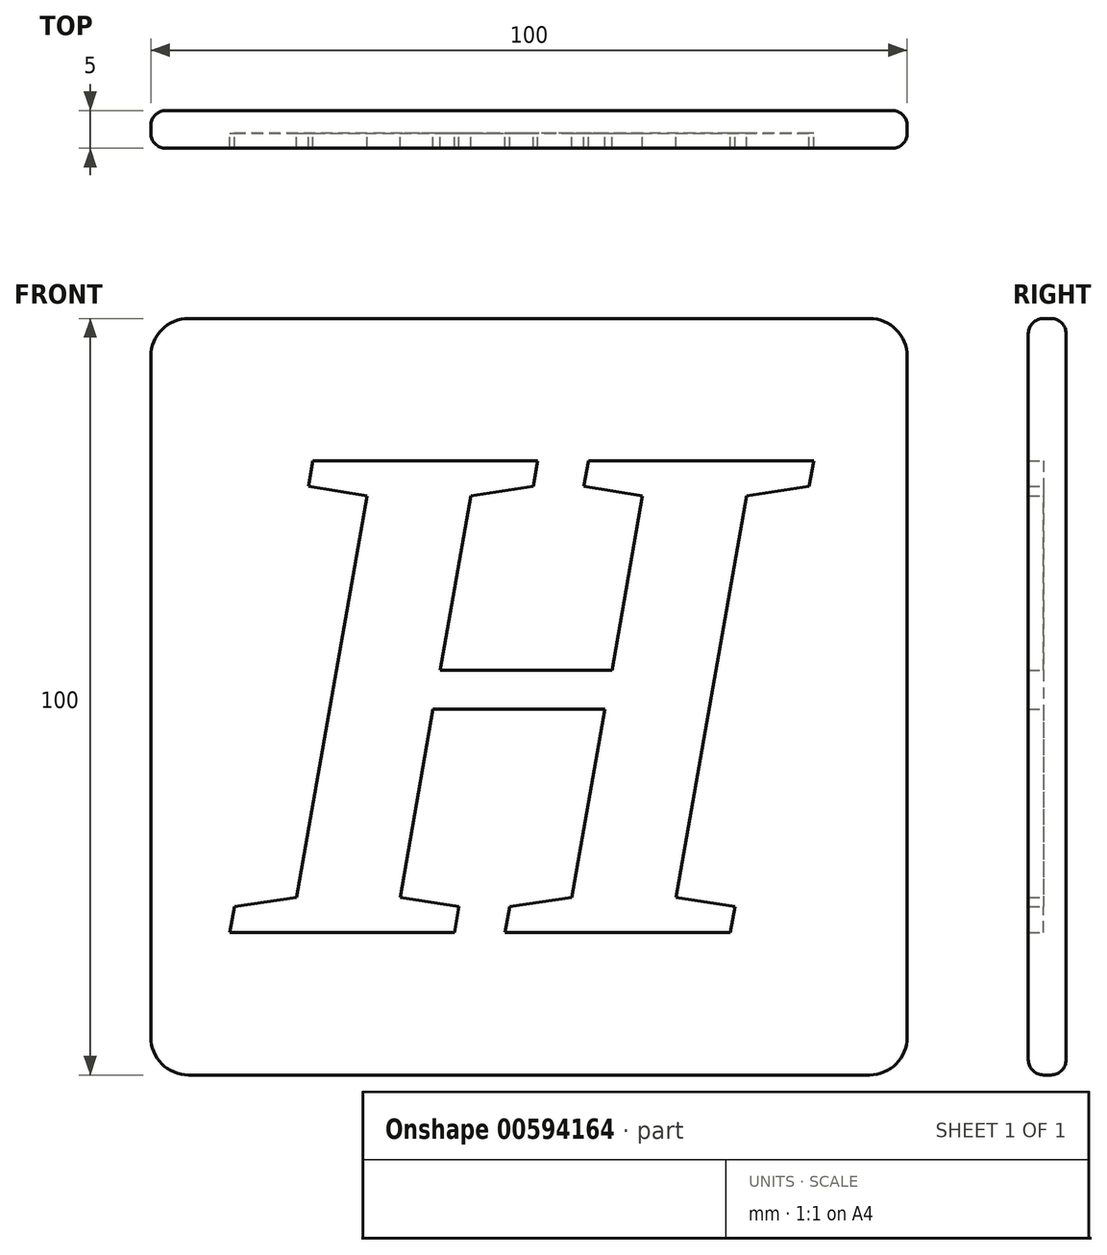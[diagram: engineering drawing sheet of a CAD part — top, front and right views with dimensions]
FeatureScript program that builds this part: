
annotation { "Feature Type Name" : "Feature", "Feature Type Description" : "" }
export const myFeature = defineFeature(function(context is Context, id is Id, definition is map)
    precondition{}
    {
        {
            var Q0;
            Q0=qCreatedBy(makeId("Front.planeOp"),FACE);
            var sketch = newSketch(context, id + "F0", { "sketchPlane" : qUnion([Q0])});
            skLineSegment(sketch, "E0.bottom", {"start": v(50, 50) * mm, "end": v(-50, 50) * mm});
            skLineSegment(sketch, "E0.top", {"start": v(50, -50) * mm, "end": v(-50, -50) * mm});
            skLineSegment(sketch, "E0.left", {"start": v(50, 50) * mm, "end": v(50, -50) * mm});
            skLineSegment(sketch, "E0.right", {"start": v(-50, 50) * mm, "end": v(-50, -50) * mm});
            skPoint(sketch, "E0.middle", {"position": v(0, 0) * mm});
            skSolve(sketch);
        }
        {
            var Q0;
            Q0=makeQuery(id+"F0.imprint","IMPRINT",FACE,{"disambiguationData":[TD([[makeQuery(id+"F0.imprint","IMPRINT",EDGE,{"derivedFrom":sQuery(id+"F0.wireOp",EDGE,"E0.bottom")}),1.0]])]});
            extrude(context, id + "F1", {"entities" : qUnion([Q0]), "depth" : 5 * mm, "offsetDistance" : 25 * mm});
        }
        {
            var Q0;
            Q0=makeQuery(id+"F1.opExtrude","SWEPT_EDGE",EDGE,{"disambiguationData":[OSD([sQuery(id+"F0.wireOp",EDGE,"E0.bottom"),sQuery(id+"F0.wireOp",EDGE,"E0.left")])]});
            var Q1;
            Q1=makeQuery(id+"F1.opExtrude","SWEPT_EDGE",EDGE,{"disambiguationData":[OSD([sQuery(id+"F0.wireOp",EDGE,"E0.bottom"),sQuery(id+"F0.wireOp",EDGE,"E0.right")])]});
            var Q2;
            Q2=makeQuery(id+"F1.opExtrude","SWEPT_EDGE",EDGE,{"disambiguationData":[OSD([sQuery(id+"F0.wireOp",EDGE,"E0.top"),sQuery(id+"F0.wireOp",EDGE,"E0.right")])]});
            var Q3;
            Q3=makeQuery(id+"F1.opExtrude","SWEPT_EDGE",EDGE,{"disambiguationData":[OSD([sQuery(id+"F0.wireOp",EDGE,"E0.top"),sQuery(id+"F0.wireOp",EDGE,"E0.left")])]});
            fillet(context, id + "F2", {"entities" : qUnion([Q0, Q1, Q2, Q3]), "radius" : 5 * mm, "tangentPropagation" : true, "allowEdgeOverflow" : false});
        }
        {
            var Q0;
            Q0=makeQuery(id+"F1.opExtrude","CAP_FACE",FACE,{"disambiguationData":[OSD([sQuery(id+"F0.wireOp",EDGE,"E0.bottom"),sQuery(id+"F0.wireOp",EDGE,"E0.top"),sQuery(id+"F0.wireOp",EDGE,"E0.left"),sQuery(id+"F0.wireOp",EDGE,"E0.right")])],"isStart":false});
            var Q1;
            Q1=makeQuery(id+"F1.opExtrude","CAP_FACE",FACE,{"disambiguationData":[OSD([sQuery(id+"F0.wireOp",EDGE,"E0.bottom"),sQuery(id+"F0.wireOp",EDGE,"E0.top"),sQuery(id+"F0.wireOp",EDGE,"E0.left"),sQuery(id+"F0.wireOp",EDGE,"E0.right")])],"isStart":true});
            fillet(context, id + "F3", {"entities" : qUnion([Q0, Q1]), "radius" : 2 * mm, "tangentPropagation" : true, "allowEdgeOverflow" : false});
        }
        {
            var Q0;
            Q0=makeQuery(id+"F1.opExtrude","CAP_FACE",FACE,{"disambiguationData":[OSD([sQuery(id+"F0.wireOp",EDGE,"E0.bottom"),sQuery(id+"F0.wireOp",EDGE,"E0.top"),sQuery(id+"F0.wireOp",EDGE,"E0.left"),sQuery(id+"F0.wireOp",EDGE,"E0.right")])],"isStart":false});
            var sketch = newSketch(context, id + "F4", { "sketchPlane" : qUnion([Q0])});
            skText(sketch, "E1", { "text": "H", "fontName": "Tinos-BoldItalic.ttf"});
            const initialGuessF4  = {"E1": [-0.03885, -0.03116, 1, 0, 0.06857]};
            skSetInitialGuess(sketch, initialGuessF4);
            skSolve(sketch);
        }
        {
            var Q0;
            Q0=makeQuery(id+"F4.imprint","IMPRINT",FACE,{"disambiguationData":[TD([[makeQuery(id+"F4.imprint","IMPRINT",EDGE,{"derivedFrom":sQuery(id+"F4.wireOp",EDGE,"E1.sketch_text.stroke-0")}),-1.0]])]});
            extrude(context, id + "F5", {"entities" : qUnion([Q0]), "operationType" : NewBodyOperationType.REMOVE, "oppositeDirection" : true, "depth" : 2 * mm, "offsetDistance" : 25 * mm});
        }
        {
            var Q0;
            Q0=makeQuery(id+"F5.boolean.opBoolean","COPY",FACE,{"derivedFrom":makeQuery(id+"F5.opExtrude","CAP_FACE",FACE,{"disambiguationData":[OSD([sQuery(id+"F4.wireOp",EDGE,"E1.sketch_text.stroke-0"),sQuery(id+"F4.wireOp",EDGE,"E1.sketch_text.stroke-1"),sQuery(id+"F4.wireOp",EDGE,"E1.sketch_text.stroke-2"),sQuery(id+"F4.wireOp",EDGE,"E1.sketch_text.stroke-3"),sQuery(id+"F4.wireOp",EDGE,"E1.sketch_text.stroke-4"),sQuery(id+"F4.wireOp",EDGE,"E1.sketch_text.stroke-5"),sQuery(id+"F4.wireOp",EDGE,"E1.sketch_text.stroke-6"),sQuery(id+"F4.wireOp",EDGE,"E1.sketch_text.stroke-7"),sQuery(id+"F4.wireOp",EDGE,"E1.sketch_text.stroke-8"),sQuery(id+"F4.wireOp",EDGE,"E1.sketch_text.stroke-9"),sQuery(id+"F4.wireOp",EDGE,"E1.sketch_text.stroke-10"),sQuery(id+"F4.wireOp",EDGE,"E1.sketch_text.stroke-11"),sQuery(id+"F4.wireOp",EDGE,"E1.sketch_text.stroke-12"),sQuery(id+"F4.wireOp",EDGE,"E1.sketch_text.stroke-13"),sQuery(id+"F4.wireOp",EDGE,"E1.sketch_text.stroke-14"),sQuery(id+"F4.wireOp",EDGE,"E1.sketch_text.stroke-15"),sQuery(id+"F4.wireOp",EDGE,"E1.sketch_text.stroke-16"),sQuery(id+"F4.wireOp",EDGE,"E1.sketch_text.stroke-17"),sQuery(id+"F4.wireOp",EDGE,"E1.sketch_text.stroke-18"),sQuery(id+"F4.wireOp",EDGE,"E1.sketch_text.stroke-19"),sQuery(id+"F4.wireOp",EDGE,"E1.sketch_text.stroke-20"),sQuery(id+"F4.wireOp",EDGE,"E1.sketch_text.stroke-21"),sQuery(id+"F4.wireOp",EDGE,"E1.sketch_text.stroke-22"),sQuery(id+"F4.wireOp",EDGE,"E1.sketch_text.stroke-23"),sQuery(id+"F4.wireOp",EDGE,"E1.sketch_text.stroke-24"),sQuery(id+"F4.wireOp",EDGE,"E1.sketch_text.stroke-25"),sQuery(id+"F4.wireOp",EDGE,"E1.sketch_text.stroke-26"),sQuery(id+"F4.wireOp",EDGE,"E1.sketch_text.stroke-27")])],"isStart":false})});
            extrude(context, id + "F6", {"entities" : qUnion([Q0]), "depth" : 2 * mm, "offsetDistance" : 25 * mm});
        }
    });
